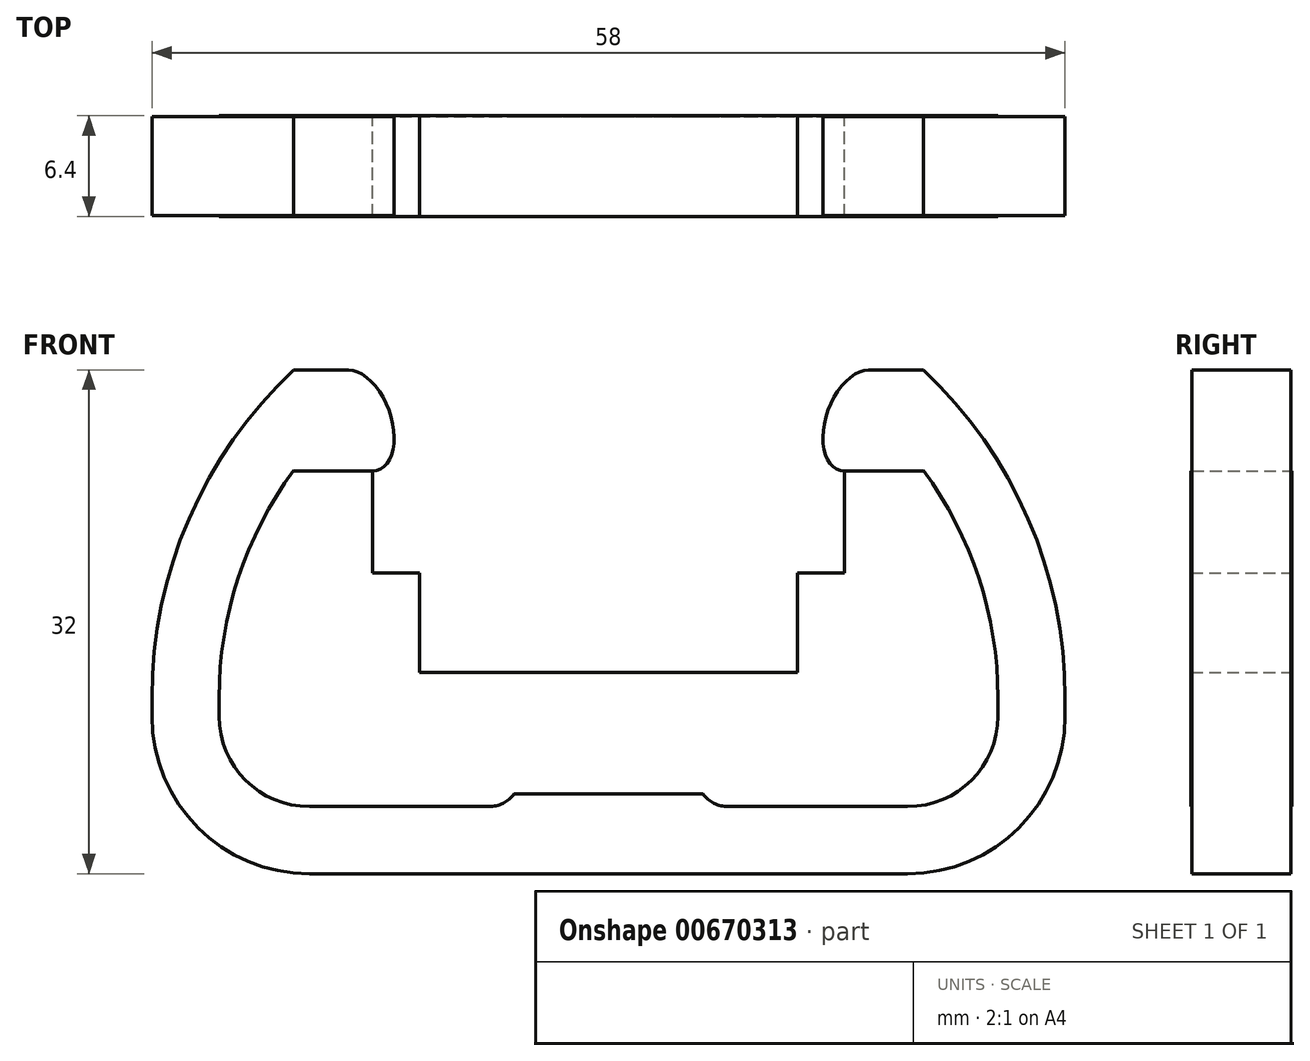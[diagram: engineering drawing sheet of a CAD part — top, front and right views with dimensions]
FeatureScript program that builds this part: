
annotation { "Feature Type Name" : "Feature", "Feature Type Description" : "" }
export const myFeature = defineFeature(function(context is Context, id is Id, definition is map)
    precondition{}
    {
        {
            assignVariable(context, id + "F0", {"name" : "thickness", "anyValue" : 6.4});
        }
        {
            var Q0;
            Q0=qCreatedBy(makeId("Front.planeOp"),FACE);
            var sketch = newSketch(context, id + "F1", { "sketchPlane" : qUnion([Q0])});
            skLineSegment(sketch, "E0", {"start": v(12, 0) * mm, "end": v(-12, 0) * mm});
            skLineSegment(sketch, "E1", {"start": v(-12, 0) * mm, "end": v(-12, 6.3) * mm});
            skLineSegment(sketch, "E2", {"start": v(-12, 6.3) * mm, "end": v(-15, 6.3) * mm});
            skLineSegment(sketch, "E3", {"start": v(-16.5, 19.2) * mm, "end": v(-20, 19.2) * mm});
            skLineSegment(sketch, "E4", {"start": v(12, 0) * mm, "end": v(12, 6.3) * mm});
            skLineSegment(sketch, "E5", {"start": v(12, 6.3) * mm, "end": v(15, 6.3) * mm});
            skLineSegment(sketch, "E6", {"start": v(16.5, 19.2) * mm, "end": v(20, 19.2) * mm});
            skLineSegment(sketch, "E7", {"start": v(-29, -1.6) * mm, "end": v(-29, -2.8) * mm});
            skLineSegment(sketch, "E8", {"start": v(29, -2.8) * mm, "end": v(29, -1.6) * mm});
            skArc(sketch, "E9", {"start": v(-29, -1.6) * mm, "mid": v(-26.65, 9.73) * mm, "end": v(-20, 19.2) * mm});
            skArc(sketch, "E10", {"start": v(29, -1.6) * mm, "mid": v(26.65, 9.73) * mm, "end": v(20, 19.2) * mm});
            skLineSegment(sketch, "E11", {"start": v(-19, -12.8) * mm, "end": v(19, -12.8) * mm});
            skPoint(sketch, "E12", {"position": v(-16.5, 19.2) * mm});
            skPoint(sketch, "E13", {"position": v(-15, 12.8) * mm});
            skLineSegment(sketch, "E14", {"start": v(-15, 12.8) * mm, "end": v(-15, 6.3) * mm});
            skPoint(sketch, "E15", {"position": v(16.5, 19.2) * mm});
            skPoint(sketch, "E16", {"position": v(15, 12.8) * mm});
            skLineSegment(sketch, "E17", {"start": v(15, 12.8) * mm, "end": v(15, 6.3) * mm});
            skPoint(sketch, "E18.visualSharp", {"position": v(-29, -12.8) * mm});
            skArc(sketch, "E18.filletArc", {"start": v(-29, -2.8) * mm, "mid": v(-26.07, -9.87) * mm, "end": v(-19, -12.8) * mm});
            skPoint(sketch, "E19.visualSharp", {"position": v(29, -12.8) * mm});
            skArc(sketch, "E19.filletArc", {"start": v(19, -12.8) * mm, "mid": v(26.07, -9.87) * mm, "end": v(29, -2.8) * mm});
            skPoint(sketch, "E20", {"position": v(-20, 12.8) * mm});
            skLineSegment(sketch, "E21", {"start": v(-20, 12.8) * mm, "end": v(-15, 12.8) * mm});
            skArc(sketch, "E22", {"start": v(-20, 12.8) * mm, "mid": v(-23.52, 5.98) * mm, "end": v(-24.73, -1.6) * mm});
            skArc(sketch, "E23", {"start": v(-24.73, -2.8) * mm, "mid": v(-23.05, -6.85) * mm, "end": v(-19, -8.53) * mm});
            skLineSegment(sketch, "E24", {"start": v(-24.73, -2.8) * mm, "end": v(-24.73, -1.6) * mm});
            skLineSegment(sketch, "E25", {"start": v(-19, -8.53) * mm, "end": v(-7.6, -8.53) * mm});
            skPoint(sketch, "E26", {"position": v(7.6, -8.53) * mm});
            skPoint(sketch, "E27", {"position": v(19, -8.53) * mm});
            skPoint(sketch, "E28", {"position": v(24.73, -2.8) * mm});
            skPoint(sketch, "E29", {"position": v(24.73, -1.6) * mm});
            skPoint(sketch, "E30", {"position": v(20, 12.8) * mm});
            skLineSegment(sketch, "E31", {"start": v(7.6, -8.53) * mm, "end": v(19, -8.53) * mm});
            skLineSegment(sketch, "E32", {"start": v(24.73, -2.8) * mm, "end": v(24.73, -1.6) * mm});
            skLineSegment(sketch, "E33", {"start": v(20, 12.8) * mm, "end": v(15, 12.8) * mm});
            skArc(sketch, "E34", {"start": v(19, -8.53) * mm, "mid": v(23.05, -6.85) * mm, "end": v(24.73, -2.8) * mm});
            skArc(sketch, "E35", {"start": v(24.73, -1.6) * mm, "mid": v(23.52, 5.98) * mm, "end": v(20, 12.8) * mm});
            skLineSegment(sketch, "E36", {"start": v(-6, -7.73) * mm, "end": v(6, -7.73) * mm});
            skEllipticalArc(sketch, "E37", {});
            skPoint(sketch, "E38", {"position": v(-13.75, 16) * mm});
            skEllipticalArc(sketch, "E39", {});
            skPoint(sketch, "E40", {"position": v(13.75, 16) * mm});
            skArc(sketch, "E41", {"start": v(-7.6, -8.53) * mm, "mid": v(-6.7, -8.32) * mm, "end": v(-6, -7.73) * mm});
            skArc(sketch, "E42", {"start": v(7.6, -8.53) * mm, "mid": v(6.7, -8.32) * mm, "end": v(6, -7.73) * mm});
            const initialGuessF1  = {"E37": [-0.01575, 0.016, 0.3437629676774163, -0.9390564530706424, 0.003334452673955964, 0.0019193554762338561, 6.075507113094146, 2.933914406837047], "E39": [0.01575, 0.016, 0.34376293961024307, 0.939056463345269, 0.0033344526525068722, 0.0019193554380365942, 0.20767817268762354, 3.34927082627742]};
            skSetInitialGuess(sketch, initialGuessF1);
            skSolve(sketch);
        }
        {
            var Q0;
            Q0=makeQuery(id+"F1.imprint","IMPRINT",FACE,{"disambiguationData":[TD([[makeQuery(id+"F1.imprint","IMPRINT",EDGE,{"derivedFrom":sQuery(id+"F1.wireOp",EDGE,"E0")}),1.0]])]});
            extrude(context, id + "F2", {"entities" : qUnion([Q0]), "endBound" : BoundingType.SYMMETRIC, "depth" : (getVariable(context, 'thickness')) * mm, "offsetDistance" : 25 * mm});
        }
        {
            var Q0;
            Q0=makeQuery(id+"F1.imprint","IMPRINT",FACE,{"disambiguationData":[TD([[makeQuery(id+"F1.imprint","IMPRINT",EDGE,{"derivedFrom":sQuery(id+"F1.wireOp",EDGE,"E3")}),1.0]])]});
            extrude(context, id + "F3", {"entities" : qUnion([Q0]), "operationType" : NewBodyOperationType.ADD, "endBound" : BoundingType.SYMMETRIC, "depth" : (getVariable(context, 'thickness') - 0.1) * mm, "offsetDistance" : 25 * mm});
        }
    });
